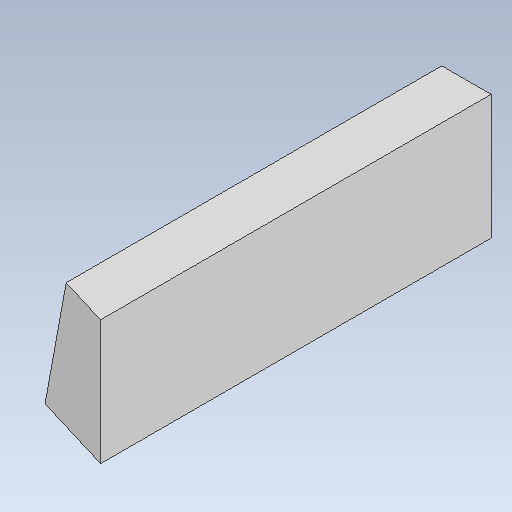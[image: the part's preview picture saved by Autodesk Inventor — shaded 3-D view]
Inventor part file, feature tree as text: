
AUTODESK INVENTOR PART (.ipt)
format: ipt  version: 2020 (Build 240168000, 168)  size: 83,456 bytes
history: native  units: in
note: dims shown in document units (in); Inventor stores cm internally (conversion verified against a paired STEP export)
features: other x3, sketch x1, plane x1
ambient origin geometry x8: Origin, YZ Plane, XZ Plane, XY Plane, X Axis, Y Axis, Z Axis, Center Point
bodies: Solid1 (feature_tree)
feature tree (5):
  other  "FrontBumperFillA.ipt"
  other  "Solid1::FrontBumperFillA.ipt"
  other  "TaggingFeature1"
  sketch  "Sketch1"  dims[d0=0.3937in]
  plane  "Work Plane1"
